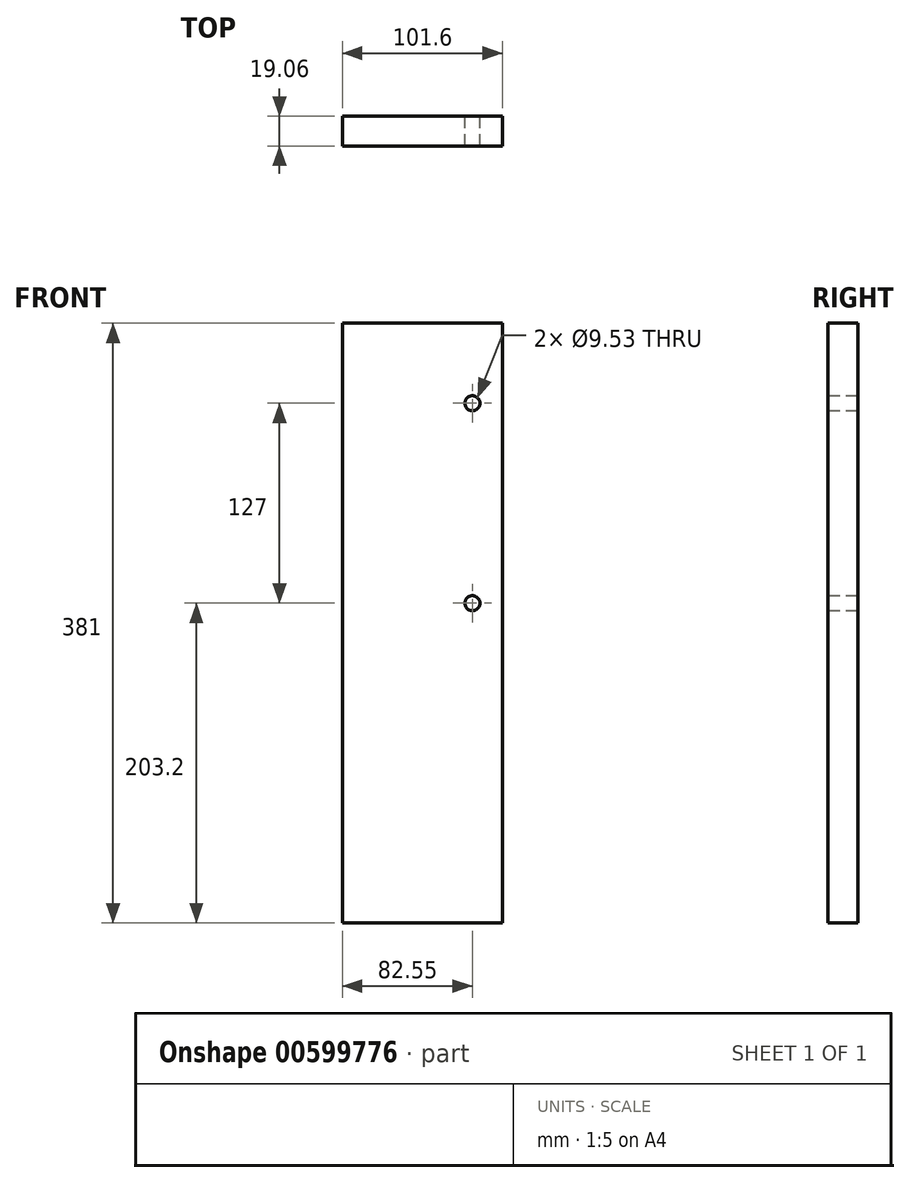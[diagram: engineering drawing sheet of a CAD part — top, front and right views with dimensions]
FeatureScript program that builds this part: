
annotation { "Feature Type Name" : "Feature", "Feature Type Description" : "" }
export const myFeature = defineFeature(function(context is Context, id is Id, definition is map)
    precondition{}
    {
        {
            var Q0;
            Q0=qCreatedBy(makeId("Front.planeOp"),FACE);
            var sketch = newSketch(context, id + "F0", { "sketchPlane" : qUnion([Q0])});
            skLineSegment(sketch, "E0.bottom", {"start": v(50.8, 190.5) * mm, "end": v(-50.8, 190.5) * mm});
            skLineSegment(sketch, "E0.top", {"start": v(50.8, -190.5) * mm, "end": v(-50.8, -190.5) * mm});
            skLineSegment(sketch, "E0.left", {"start": v(50.8, 190.5) * mm, "end": v(50.8, -190.5) * mm});
            skLineSegment(sketch, "E0.right", {"start": v(-50.8, 190.5) * mm, "end": v(-50.8, -190.5) * mm});
            skPoint(sketch, "E0.middle", {"position": v(0, 0) * mm});
            skLineSegment(sketch, "E1", {"start": v(0, 190.5) * mm, "end": v(0, -190.5) * mm, "construction": true});
            skCircle(sketch, "E2", {"center": v(31.75, 139.7) * mm, "radius": 4.76 * mm});
            skCircle(sketch, "E3", {"center": v(31.75, 12.7) * mm, "radius": 4.76 * mm});
            skLineSegment(sketch, "E4", {"start": v(31.75, 190.5) * mm, "end": v(31.75, -190.5) * mm, "construction": true});
            skSolve(sketch);
        }
        {
            var Q0;
            Q0 = qSketchRegion(id + "F0", true);
            extrude(context, id + "F1", {"entities" : qUnion([Q0]), "endBound" : BoundingType.SYMMETRIC, "depth" : 19.05 * mm, "offsetDistance" : 25.4 * mm});
        }
    });
